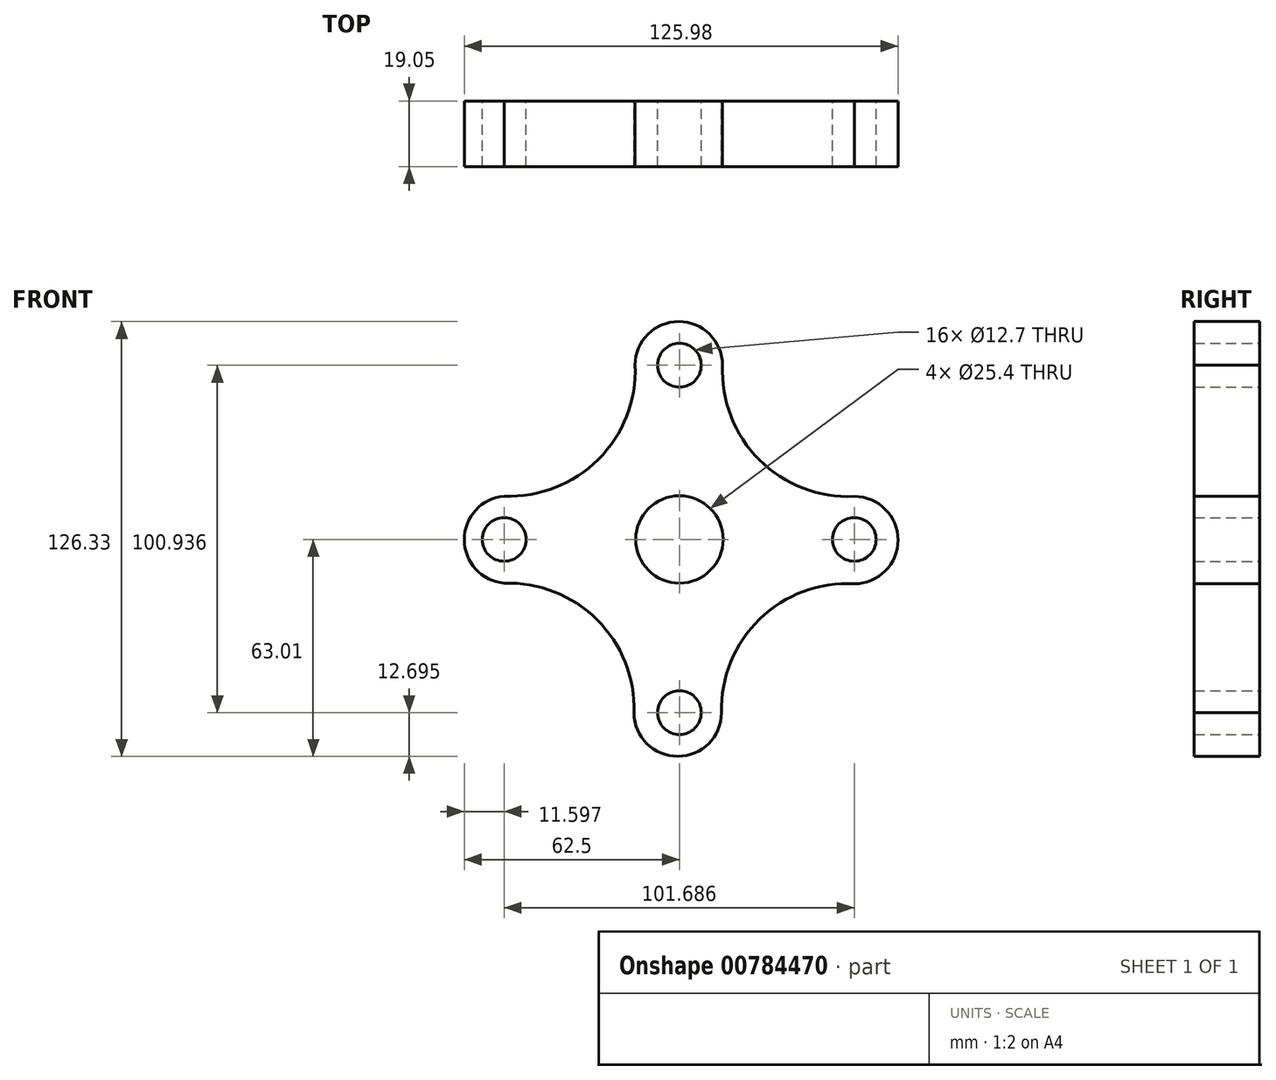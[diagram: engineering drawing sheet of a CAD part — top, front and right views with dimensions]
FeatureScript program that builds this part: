
annotation { "Feature Type Name" : "Feature", "Feature Type Description" : "" }
export const myFeature = defineFeature(function(context is Context, id is Id, definition is map)
    precondition{}
    {
        {
            var Q0;
            Q0=qCreatedBy(makeId("Front.planeOp"),FACE);
            var sketch = newSketch(context, id + "F0", { "sketchPlane" : qUnion([Q0])});
            skCircle(sketch, "E0", {"center": v(0, 0) * mm, "radius": 12.7 * mm});
            skLineSegment(sketch, "E1", {"start": v(0, 0) * mm, "end": v(0, -50.31) * mm});
            skLineSegment(sketch, "E2", {"start": v(0, 0) * mm, "end": v(0, 50.62) * mm});
            skLineSegment(sketch, "E3", {"start": v(0, 0) * mm, "end": v(50.78, 0) * mm});
            skLineSegment(sketch, "E4", {"start": v(0, 0) * mm, "end": v(-50.9, 0) * mm});
            skCircle(sketch, "E5", {"center": v(-50.9, 0) * mm, "radius": 6.35 * mm});
            skCircle(sketch, "E6", {"center": v(0, -50.31) * mm, "radius": 6.35 * mm});
            skCircle(sketch, "E7", {"center": v(50.78, 0) * mm, "radius": 6.35 * mm});
            skCircle(sketch, "E8", {"center": v(0, 50.62) * mm, "radius": 6.35 * mm});
            skLineSegment(sketch, "E9", {"start": v(-50.9, 0) * mm, "end": v(-62.5, 0) * mm});
            skLineSegment(sketch, "E10", {"start": v(0, -50.31) * mm, "end": v(0, -63) * mm});
            skLineSegment(sketch, "E11", {"start": v(50.78, 0) * mm, "end": v(63.48, 0) * mm});
            skLineSegment(sketch, "E12", {"start": v(0, 50.62) * mm, "end": v(0, 63.32) * mm});
            skLineSegment(sketch, "E13", {"start": v(0, 50.62) * mm, "end": v(12.52, 50.62) * mm});
            skLineSegment(sketch, "E14", {"start": v(12.52, 50.62) * mm, "end": v(-12.88, 50.62) * mm});
            skLineSegment(sketch, "E15", {"start": v(50.78, 0) * mm, "end": v(50.78, 12.51) * mm});
            skLineSegment(sketch, "E16", {"start": v(50.78, 12.51) * mm, "end": v(50.78, -12.89) * mm});
            skLineSegment(sketch, "E17", {"start": v(-50.9, 0) * mm, "end": v(-50.9, 12.6) * mm});
            skLineSegment(sketch, "E18", {"start": v(-50.9, 12.6) * mm, "end": v(-50.9, -12.7) * mm});
            skLineSegment(sketch, "E19", {"start": v(0, -50.31) * mm, "end": v(-13.19, -50.31) * mm});
            skLineSegment(sketch, "E20", {"start": v(-13.19, -50.31) * mm, "end": v(12.21, -50.31) * mm});
            skArc(sketch, "E21", {"start": v(12.52, 50.62) * mm, "mid": v(-0.18, 63.32) * mm, "end": v(-12.88, 50.62) * mm});
            skArc(sketch, "E22", {"start": v(50.78, -12.89) * mm, "mid": v(63.48, -0.19) * mm, "end": v(50.78, 12.51) * mm});
            skArc(sketch, "E23", {"start": v(-50.9, 12.6) * mm, "mid": v(-62.5, -0.05) * mm, "end": v(-50.9, -12.7) * mm});
            skArc(sketch, "E24", {"start": v(-13.19, -50.31) * mm, "mid": v(-0.49, -63.01) * mm, "end": v(12.21, -50.31) * mm});
            skArc(sketch, "E25", {"start": v(-50.9, 12.6) * mm, "mid": v(-23.54, 23.26) * mm, "end": v(-12.88, 50.62) * mm});
            skArc(sketch, "E26", {"start": v(12.52, 50.62) * mm, "mid": v(23.23, 23.11) * mm, "end": v(50.78, 12.51) * mm});
            skArc(sketch, "E27", {"start": v(-13.19, -50.31) * mm, "mid": v(-23.9, -23.34) * mm, "end": v(-50.9, -12.7) * mm});
            skArc(sketch, "E28", {"start": v(50.78, -12.89) * mm, "mid": v(23.29, -23.14) * mm, "end": v(12.21, -50.31) * mm});
            skSolve(sketch);
        }
        {
            var Q0;
            Q0 = qSketchRegion(id + "F0", true);
            extrude(context, id + "F1", {"entities" : qUnion([Q0]), "depth" : 19.05 * mm, "offsetDistance" : 25.4 * mm});
        }
    });
